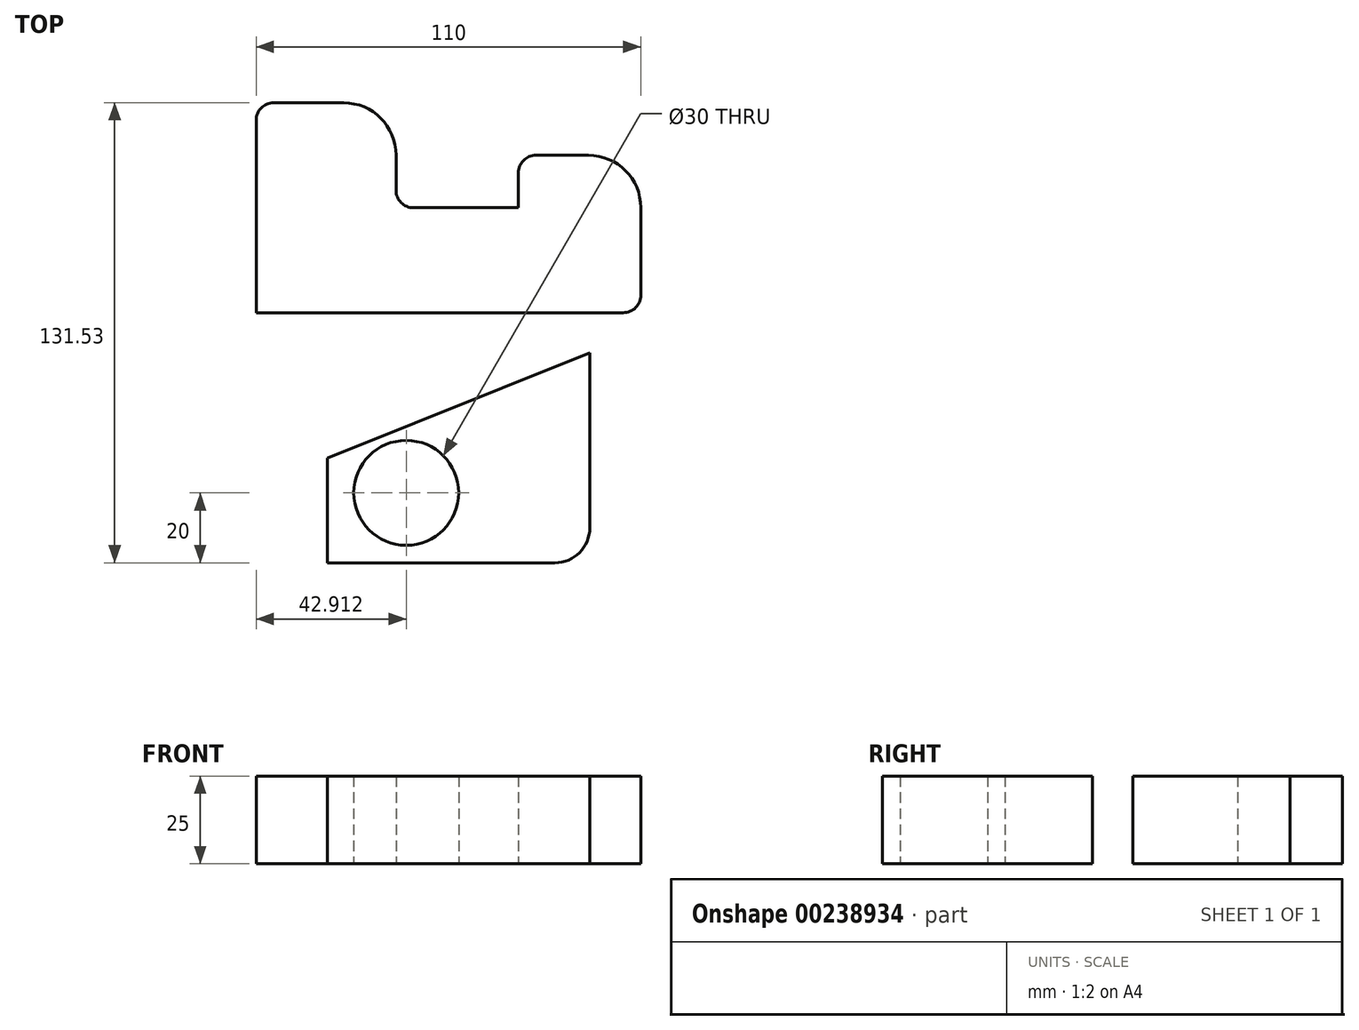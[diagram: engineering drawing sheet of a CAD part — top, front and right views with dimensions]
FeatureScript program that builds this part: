
annotation { "Feature Type Name" : "Feature", "Feature Type Description" : "" }
export const myFeature = defineFeature(function(context is Context, id is Id, definition is map)
    precondition{}
    {
        {
            var Q0;
            Q0=qCreatedBy(makeId("Top.planeOp"),FACE);
            var sketch = newSketch(context, id + "F0", { "sketchPlane" : qUnion([Q0])});
            skLineSegment(sketch, "E0", {"start": v(-43.33, -60) * mm, "end": v(21.67, -60) * mm});
            skLineSegment(sketch, "E1", {"start": v(31.67, -50) * mm, "end": v(31.67, 0) * mm});
            skPoint(sketch, "E2.visualSharp", {"position": v(31.67, -60) * mm});
            skArc(sketch, "E2.filletArc", {"start": v(21.67, -60) * mm, "mid": v(28.74, -57.07) * mm, "end": v(31.67, -50) * mm});
            skLineSegment(sketch, "E3", {"start": v(-43.33, -60) * mm, "end": v(-43.33, -30) * mm});
            skLineSegment(sketch, "E4", {"start": v(-43.33, -30) * mm, "end": v(31.67, 0) * mm});
            skCircle(sketch, "E5", {"center": v(-20.83, -40) * mm, "radius": 15 * mm});
            skLineSegment(sketch, "E6", {"start": v(-63.74, 11.53) * mm, "end": v(41.26, 11.53) * mm});
            skLineSegment(sketch, "E7", {"start": v(-63.74, 11.53) * mm, "end": v(-63.74, 66.53) * mm});
            skLineSegment(sketch, "E8", {"start": v(-58.74, 71.53) * mm, "end": v(-38.74, 71.53) * mm});
            skLineSegment(sketch, "E9", {"start": v(-23.74, 56.53) * mm, "end": v(-23.74, 46.53) * mm});
            skLineSegment(sketch, "E10", {"start": v(-18.74, 41.53) * mm, "end": v(11.26, 41.53) * mm});
            skLineSegment(sketch, "E11", {"start": v(11.26, 41.53) * mm, "end": v(11.26, 51.53) * mm});
            skLineSegment(sketch, "E12", {"start": v(16.26, 56.53) * mm, "end": v(31.26, 56.53) * mm});
            skLineSegment(sketch, "E13", {"start": v(46.26, 41.53) * mm, "end": v(46.26, 16.53) * mm});
            skPoint(sketch, "E14.visualSharp", {"position": v(-63.74, 71.53) * mm});
            skArc(sketch, "E14.filletArc", {"start": v(-58.74, 71.53) * mm, "mid": v(-62.27, 70.06) * mm, "end": v(-63.74, 66.53) * mm});
            skPoint(sketch, "E15.visualSharp", {"position": v(-23.74, 41.53) * mm});
            skArc(sketch, "E15.filletArc", {"start": v(-23.74, 46.53) * mm, "mid": v(-22.27, 43) * mm, "end": v(-18.74, 41.53) * mm});
            skPoint(sketch, "E16.visualSharp", {"position": v(-23.74, 71.53) * mm});
            skArc(sketch, "E16.filletArc", {"start": v(-23.74, 56.53) * mm, "mid": v(-28.13, 67.13) * mm, "end": v(-38.74, 71.53) * mm});
            skPoint(sketch, "E17.visualSharp", {"position": v(11.26, 56.53) * mm});
            skArc(sketch, "E17.filletArc", {"start": v(16.26, 56.53) * mm, "mid": v(12.73, 55.06) * mm, "end": v(11.26, 51.53) * mm});
            skPoint(sketch, "E18.visualSharp", {"position": v(46.26, 56.53) * mm});
            skArc(sketch, "E18.filletArc", {"start": v(46.26, 41.53) * mm, "mid": v(41.87, 52.13) * mm, "end": v(31.26, 56.53) * mm});
            skPoint(sketch, "E19.visualSharp", {"position": v(46.26, 11.53) * mm});
            skArc(sketch, "E19.filletArc", {"start": v(41.26, 11.53) * mm, "mid": v(44.8, 13) * mm, "end": v(46.26, 16.53) * mm});
            skSolve(sketch);
        }
        {
            var Q0;
            Q0 = qSketchRegion(id + "F0", true);
            extrude(context, id + "F1", {"entities" : qUnion([Q0]), "depth" : 25 * mm});
        }
    });
